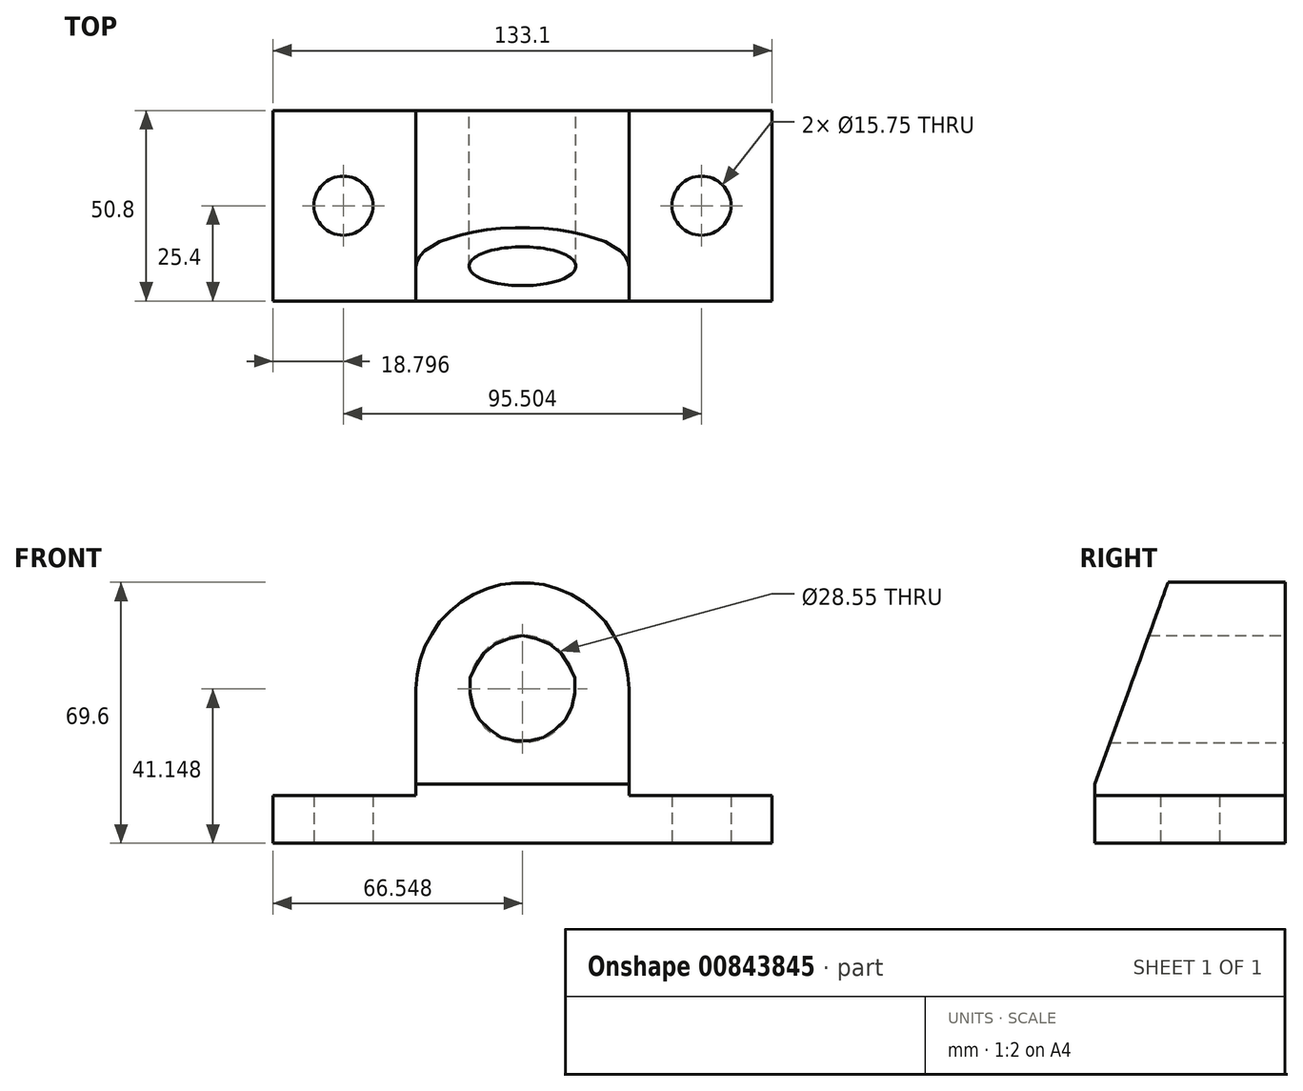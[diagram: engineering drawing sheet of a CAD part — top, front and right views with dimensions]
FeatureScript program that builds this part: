
annotation { "Feature Type Name" : "Feature", "Feature Type Description" : "" }
export const myFeature = defineFeature(function(context is Context, id is Id, definition is map)
    precondition{}
    {
        {
            var Q0;
            Q0=qCreatedBy(makeId("Top.planeOp"),FACE);
            var sketch = newSketch(context, id + "F0", { "sketchPlane" : qUnion([Q0])});
            skLineSegment(sketch, "E0.left", {"start": v(0, 0) * mm, "end": v(0, 50.8) * mm});
            skLineSegment(sketch, "E0.right", {"start": v(133.1, 0) * mm, "end": v(133.1, 50.8) * mm});
            skLineSegment(sketch, "E1", {"start": v(95, 0) * mm, "end": v(95, 50.8) * mm});
            skLineSegment(sketch, "E2", {"start": v(38.1, 0) * mm, "end": v(38.1, 50.8) * mm});
            skLineSegment(sketch, "E3", {"start": v(0, 0) * mm, "end": v(133.1, 0) * mm});
            skLineSegment(sketch, "E4", {"start": v(0, 50.8) * mm, "end": v(133.1, 50.8) * mm});
            skLineSegment(sketch, "E5", {"start": v(66.55, 0) * mm, "end": v(114.3, 0) * mm});
            skLineSegment(sketch, "E6", {"start": v(66.55, 0) * mm, "end": v(18.8, 0) * mm});
            skLineSegment(sketch, "E7", {"start": v(18.8, 0) * mm, "end": v(18.8, 25.4) * mm});
            skLineSegment(sketch, "E8", {"start": v(114.3, 0) * mm, "end": v(114.3, 25.4) * mm});
            skCircle(sketch, "E9", {"center": v(18.8, 25.4) * mm, "radius": 7.87 * mm});
            skCircle(sketch, "E10", {"center": v(114.3, 25.4) * mm, "radius": 7.87 * mm});
            skSolve(sketch);
        }
        {
            var Q0;
            Q0=makeQuery(id+"F0.imprint","IMPRINT",FACE,{"disambiguationData":[TD([[makeQuery(id+"F0.imprint","IMPRINT",EDGE,{"derivedFrom":sQuery(id+"F0.wireOp",EDGE,"E0.bottom")}),1.0]])]});
            var Q1;
            {var subQ0=sQuery(id+"F0.wireOp",EDGE,"E0.right");Q1=makeQuery(id+"F0.imprint","IMPRINT",FACE,{"disambiguationData":[TD([[makeQuery(id+"F0.imprint","IMPRINT",EDGE,{"derivedFrom":subQ0}),1.0]])]});}
            var Q2;
            Q2=makeQuery(id+"F0.imprint","IMPRINT",FACE,{"disambiguationData":[TD([[makeQuery(id+"F0.imprint","IMPRINT",EDGE,{"derivedFrom":sQuery(id+"F0.wireOp",EDGE,"tcfTvVFN-FUT2-oFyI-7aY5-GAKvWrabjyyD.top")}),-1.0]])]});
            var Q3;
            {var subQ0=sQuery(id+"F0.wireOp",EDGE,"E0.left");Q3=makeQuery(id+"F0.imprint","IMPRINT",FACE,{"disambiguationData":[TD([[makeQuery(id+"F0.imprint","IMPRINT",EDGE,{"derivedFrom":subQ0}),-1.0]])]});}
            var Q4;
            {var subQ0=sQuery(id+"F0.wireOp",EDGE,"E1");Q4=makeQuery(id+"F0.imprint","IMPRINT",FACE,{"disambiguationData":[TD([[makeQuery(id+"F0.imprint","IMPRINT",EDGE,{"derivedFrom":subQ0}),1.0]])]});}
            extrude(context, id + "F1", {"entities" : qUnion([Q0, Q1, Q2, Q3, Q4]), "depth" : 12.7 * mm, "offsetDistance" : 25.4 * mm});
        }
        {
            var Q0;
            {var subQ0=sQuery(id+"F0.wireOp",EDGE,"E1");Q0=makeQuery(id+"F0.imprint","IMPRINT",FACE,{"disambiguationData":[TD([[makeQuery(id+"F0.imprint","IMPRINT",EDGE,{"derivedFrom":subQ0}),1.0]])]});}
            extrude(context, id + "F2", {"entities" : qUnion([Q0]), "operationType" : NewBodyOperationType.ADD, "depth" : 15.75 * mm, "offsetDistance" : 25.4 * mm});
        }
        {
            var Q0;
            Q0=makeQuery(id+"F2.opExtrude","CAP_FACE",FACE,{"disambiguationData":[OSD([sQuery(id+"F0.wireOp",EDGE,"E1"),sQuery(id+"F0.wireOp",EDGE,"E2"),sQuery(id+"F0.wireOp",EDGE,"E3"),sQuery(id+"F0.wireOp",EDGE,"E4")])],"isStart":false});
            var sketch = newSketch(context, id + "F3", { "sketchPlane" : qUnion([Q0])});
            skSolve(sketch);
        }
        {
            var Q0;
            Q0=makeQuery(id+"F3.imprint","IMPRINT",FACE,{"disambiguationData":[TD([[makeQuery(id+"F3.imprint","IMPRINT",EDGE,{"derivedFrom":makeQuery(id+"F2.opExtrude","CAP_EDGE",EDGE,{"disambiguationData":[OSD([sQuery(id+"F0.wireOp",EDGE,"E1")])],"isStart":false})}),1.0]])]});
            extrude(context, id + "F4", {"entities" : qUnion([Q0]), "operationType" : NewBodyOperationType.ADD, "depth" : 25.4 * mm, "offsetDistance" : 25.4 * mm});
        }
        {
            var Q0;
            Q0=makeQuery(id+"F0.imprint","IMPRINT",FACE,{"disambiguationData":[TD([[makeQuery(id+"F0.imprint","IMPRINT",EDGE,{"derivedFrom":sQuery(id+"F0.wireOp",EDGE,"E9")}),1.0]])]});
            var Q1;
            Q1=makeQuery(id+"F0.imprint","IMPRINT",FACE,{"disambiguationData":[TD([[makeQuery(id+"F0.imprint","IMPRINT",EDGE,{"derivedFrom":sQuery(id+"F0.wireOp",EDGE,"E10")}),1.0]])]});
            extrude(context, id + "F5", {"entities" : qUnion([Q0, Q1]), "operationType" : NewBodyOperationType.REMOVE, "oppositeDirection" : true, "depth" : 47.24 * mm, "offsetDistance" : 25.4 * mm});
        }
        {
            var Q0;
            {var subQ0=sQuery(id+"F0.wireOp",EDGE,"E4");Q0=makeQuery(id+"F4.boolean.opBoolean","MERGE",FACE,{"derivedFrom":[makeQuery(id+"F2.boolean.opBoolean","MERGE",FACE,{"derivedFrom":[makeQuery(id+"F1.opExtrude","SWEPT_FACE",FACE,{"disambiguationData":[OSD([subQ0])]}),makeQuery(id+"F2.opExtrude","SWEPT_FACE",FACE,{"disambiguationData":[OSD([subQ0])]})]}),makeQuery(id+"F4.opExtrude","SWEPT_FACE",FACE,{"disambiguationData":[OSD([subQ0])]})]});}
            var sketch = newSketch(context, id + "F6", { "sketchPlane" : qUnion([Q0])});
            skCircle(sketch, "E11", {"center": v(-66.55, 41.15) * mm, "radius": 28.45 * mm});
            skCircle(sketch, "E12", {"center": v(-66.55, 41.15) * mm, "radius": 14.27 * mm});
            skSolve(sketch);
        }
        {
            var Q0;
            {var subQ1=sQuery(id+"F0.wireOp",EDGE,"E4");var subQ3=makeQuery(id+"F4.opExtrude","CAP_EDGE",EDGE,{"disambiguationData":[OSD([subQ1])],"isStart":false});var subQ7=sQuery(id+"F6.wireOp",EDGE,"E12");var subQ8=makeQuery(id+"F6.imprint","INTERSECT",VERTEX,{"disambiguationData":[OD(0.0)],"derivedFrom":[subQ3,subQ7]});Q0=makeQuery(id+"F6.imprint","IMPRINT",FACE,{"disambiguationData":[TD([[makeQuery(id+"F6.imprint","IMPRINT",EDGE,{"disambiguationData":[TD([[subQ8,1.0]])],"derivedFrom":subQ7}),-1.0]])]});}
            extrude(context, id + "F7", {"entities" : qUnion([Q0]), "operationType" : NewBodyOperationType.ADD, "oppositeDirection" : true, "depth" : 50.8 * mm, "offsetDistance" : 25.4 * mm});
        }
        {
            var Q0;
            {var subQ0=sQuery(id+"F6.wireOp",EDGE,"E12");var subQ1=makeQuery(id+"F4.opExtrude","CAP_EDGE",EDGE,{"disambiguationData":[OSD([sQuery(id+"F0.wireOp",EDGE,"E4")])],"isStart":false});var subQ2=makeQuery(id+"F6.imprint","INTERSECT",VERTEX,{"disambiguationData":[OD(0.0)],"derivedFrom":[subQ1,subQ0]});Q0=makeQuery(id+"F6.imprint","IMPRINT",FACE,{"disambiguationData":[TD([[makeQuery(id+"F6.imprint","IMPRINT",EDGE,{"disambiguationData":[TD([[subQ2,-1.0]])],"derivedFrom":subQ0}),1.0]])]});}
            extrude(context, id + "F8", {"entities" : qUnion([Q0]), "operationType" : NewBodyOperationType.REMOVE, "oppositeDirection" : true, "depth" : 50.8 * mm, "offsetDistance" : 25.4 * mm});
        }
        {
            var Q0;
            {var subQ0=sQuery(id+"F0.wireOp",EDGE,"E1");Q0=makeQuery(id+"F4.boolean.opBoolean","MERGE",FACE,{"derivedFrom":[makeQuery(id+"F2.opExtrude","SWEPT_FACE",FACE,{"disambiguationData":[OSD([subQ0])]}),makeQuery(id+"F4.opExtrude","SWEPT_FACE",FACE,{"disambiguationData":[OSD([subQ0])]})]});}
            var sketch = newSketch(context, id + "F9", { "sketchPlane" : qUnion([Q0])});
            skLineSegment(sketch, "E13", {"start": v(0, 12.7) * mm, "end": v(0, 15.75) * mm});
            skLineSegment(sketch, "E14", {"start": v(0, 15.75) * mm, "end": v(50.8, 15.75) * mm});
            skLineSegment(sketch, "E15", {"start": v(0, 15.75) * mm, "end": v(0, 68.75) * mm});
            skLineSegment(sketch, "E16", {"start": v(0, 68.75) * mm, "end": v(0, 86.04) * mm});
            skLineSegment(sketch, "E17", {"start": v(0, 86.04) * mm, "end": v(25.58, 86.04) * mm});
            skLineSegment(sketch, "E18", {"start": v(0, 15.75) * mm, "end": v(25.58, 86.04) * mm});
            skSolve(sketch);
        }
        {
            var Q0;
            {var subQ5=sQuery(id+"F9.wireOp",EDGE,"E16");Q0=makeQuery(id+"F9.imprint","IMPRINT",FACE,{"disambiguationData":[TD([[makeQuery(id+"F9.imprint","IMPRINT",EDGE,{"derivedFrom":subQ5}),-1.0]])]});}
            var Q1;
            {var subQ0=sQuery(id+"F9.wireOp",EDGE,"E15");var subQ4=sQuery(id+"F9.wireOp",EDGE,"E18");var subQ5=makeQuery(id+"F9.imprint","INTERSECT",VERTEX,{"derivedFrom":[sQuery(id+"F9.wireOp",EDGE,"E13"),sQuery(id+"F9.wireOp",EDGE,"E14"),subQ0,subQ4]});Q1=makeQuery(id+"F9.imprint","IMPRINT",FACE,{"disambiguationData":[TD([[makeQuery(id+"F9.imprint","IMPRINT",EDGE,{"disambiguationData":[TD([[subQ5,1.0]])],"derivedFrom":subQ0}),1.0]])]});}
            extrude(context, id + "F10", {"entities" : qUnion([Q0, Q1]), "operationType" : NewBodyOperationType.REMOVE, "oppositeDirection" : true, "depth" : 101.6 * mm, "offsetDistance" : 25.4 * mm});
        }
    });
